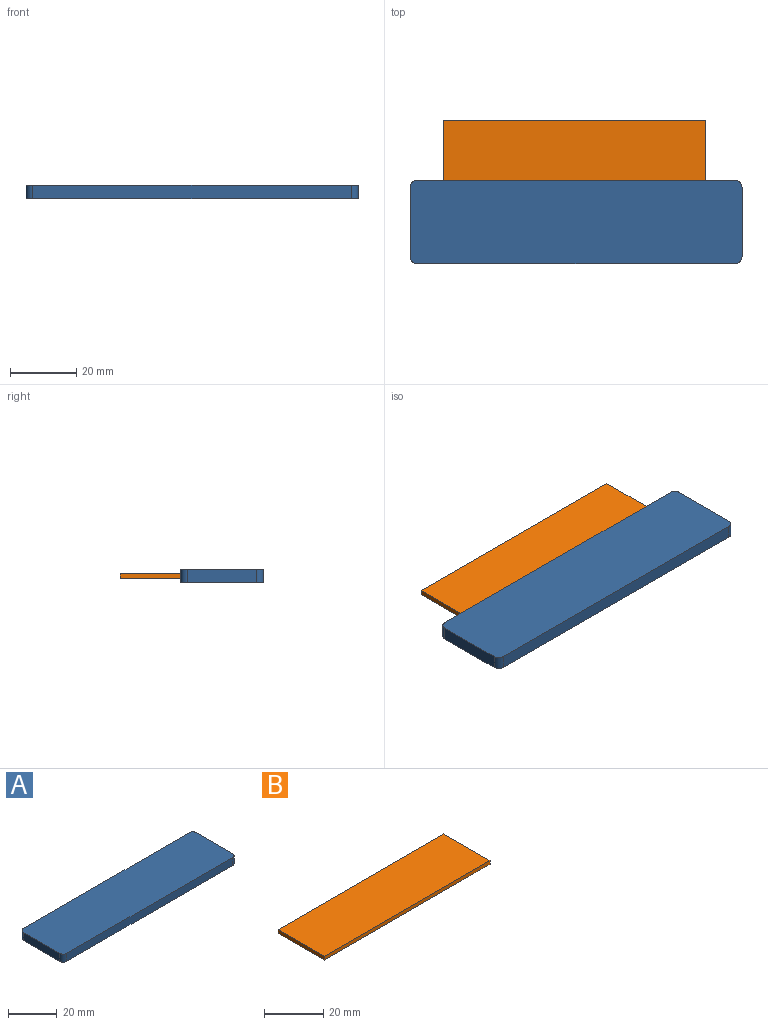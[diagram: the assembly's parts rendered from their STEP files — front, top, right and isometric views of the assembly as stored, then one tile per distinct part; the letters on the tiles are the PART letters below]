
ASSEMBLY  parts=2 mates=1
PART A: 18 faces, bbox 100x25x4 mm
  f0: plane 96x4mm, normal (0,1,0), area 155.4mm2, adj f4,f5,f6,f7,f9,f11,f12,f13
  f1: plane 21x4mm, normal (-1,0,0), area 84mm2, adj f4,f12,f14,f15
  f2: plane 96x4mm, normal (0,-1,0), area 384mm2, adj f4,f12,f15,f16
  f3: plane 21x4mm, normal (1,0,0), area 84mm2, adj f4,f12,f16,f17
  f4: plane 100x25mm, normal (0,0,-1), area 1023.9mm2, adj f0,f1,f2,f3,f9,f10,f11,f14
  f5: plane 23x1.94mm, normal (1,0,0), area 44.6mm2, adj f0,f6,f8,f13
  f6: plane 80.8x23mm, normal (0,0,-1), area 1858.3mm2, adj f0,f5,f7,f8
  f7: plane 23x1.94mm, normal (-1,0,0), area 44.6mm2, adj f0,f6,f8,f13
  f8: plane 80.8x1.94mm, normal (0,1,0), area 156.8mm2, adj f5,f6,f7,f13
  f9: plane 20.95x1.02mm, normal (-1,0,0), area 21.4mm2, adj f0,f4,f10,f13
  f10: plane 70.31x1.02mm, normal (0,1,0), area 71.8mm2, adj f4,f9,f11,f13
  f11: plane 20.95x1.02mm, normal (1,0,0), area 21.4mm2, adj f0,f4,f10,f13
  f12: plane 100x25mm, normal (0,0,1), area 2496.6mm2, adj f0,f1,f2,f3,f14,f15,f16,f17
  f13: plane 80.8x23mm, normal (0,0,1), area 385.6mm2, adj f0,f5,f7,f8,f9,f10,f11
  f14: cylinder r=2mm len=4mm, axis (0,0,1), area 12.6mm2, adj f0,f1,f4,f12
  f15: cylinder r=2mm len=4mm, axis (0,0,-1), area 12.6mm2, adj f1,f2,f4,f12
  f16: cylinder r=2mm len=4mm, axis (0,0,1), area 12.6mm2, adj f2,f3,f4,f12
  f17: cylinder r=2mm len=4mm, axis (0,0,-1), area 12.6mm2, adj f0,f3,f4,f12
PART B: 6 faces, bbox 79x22x1.5 mm
  f0: plane 79x1.5mm, normal (0,1,0), area 118.5mm2, adj f1,f3,f4,f5
  f1: plane 22x1.5mm, normal (-1,0,0), area 33mm2, adj f0,f2,f3,f4
  f2: plane 79x1.5mm, normal (0,-1,0), area 118.5mm2, adj f1,f3,f4,f5
  f3: plane 79x22mm, normal (0,0,1), area 1738mm2, adj f0,f1,f2,f5
  f4: plane 79x22mm, normal (0,0,-1), area 1738mm2, adj f0,f1,f2,f5
  f5: plane 22x1.5mm, normal (1,0,0), area 33mm2, adj f0,f2,f3,f4
PLACE A t=(-47.4,50.49,-1.24)mm
PLACE B t=(0,19.1,0)mm
MATE slider A.f8 <-> B.f2  axis (0,1,0) through (-7,27.02,0.75)mm
